# Revit family: NBS_PineappleContracts_DmstcChrs_RynoStool
name_source: partatom
category: Furniture
revit_build: Autodesk Revit 2018 (Build: 20190510_1515(x64)
units: mm (PartAtom-declared; Revit-internal decimal feet)

## family parameters
Always vertical = Yes
Cut with Voids When Loaded = No
Room Calculation Point = No
Shared = No
Work Plane-Based = No

## types (1)
- RynoStool
    AssetType = Fixed
    BIMObjectName = NBS_PineappleContracts_DomesticChairs_RynoStool
    Category = Pr_40_50_12_85:Stools
    CodePerformance = BS EN 16139: 2013 level 2, BS 5852:2006, UL94 HB flammability standards
    Color = Blaze orange, epic blue, icon purple, vegas yellow, cool green, black, thunder grey, moonwalk grey, lime green, granite
    Depth = 396 mm  [stored 1.29921 ft]
    Description = Ryno stool
    DurationUnit = year
    Features = Weatherproof, fire retardant, floor fixing option available
    Height = 470 mm  [stored 1.54199 ft]
    HighestSeatingHeight = 470 mm  [stored 1.54199 ft]
    IfcExportAs = IfcFurnitureType
    IfcExportType = CHAIR
    IsBuiltIn = No
    LowestSeatingHeight = 470 mm  [stored 1.54199 ft]
    ManufacturerName = Pineapple Contracts
    ManufacturerURL = www.pineapplecontracts.com
    Material = UV stabilised polyethylene with anti-microbial additive
    ModelNumber = 1RYS-FF-50
    ModelReference = RynoStool
    NBSCertification = www.nationalbimlibrary.com/cert/lfek0bag
    NBSDescription = Domestic chairs
    NBSReference = 45-35-20/365
    Name = DomesticChairs_RynoStool_PineappleContracts
    NominalDepth = 396 mm  [stored 1.29921 ft]
    NominalHeight = 470 mm  [stored 1.54199 ft]
    NominalLength = 0 mm  [stored 0 ft]
    NominalWidth = 445 mm  [stored 1.45997 ft]
    ProductInformation = https://uk.pineapplecontracts.com
    SeatingHeight = 470 mm  [stored 1.54199 ft]
    Shape = Cylinder
    Size = 470 x 445 x 396 mm
    Status = UNSET
    StoolMaterial = NBS_PineappleContracts_IconPurple
    Style = Stool
    SustainabilityPerformance = 100% recyclable
    Uniclass2015Code = Pr_40_50_12_85
    Uniclass2015Title = Stools
    Uniclass2015Version = Products v1.15
    Version = 2
    WarrantyDescription = Lifetime guarantee against manufacturing faults
    WarrantyDurationUnit = year
    WeightOptions = 50 kg standard model, 25 kg midweight model, 5 kg lightweight model, contact manufacturer for additional weight options
    Width = 445 mm  [stored 1.45997 ft]

note: [stored X ft] marks values corroborated as IEEE doubles in the binary element streams (Revit-internal decimal feet)

## geometry (parser evidence)
native form markers: Sweep x2
no freeform markers — native parametric forms only
